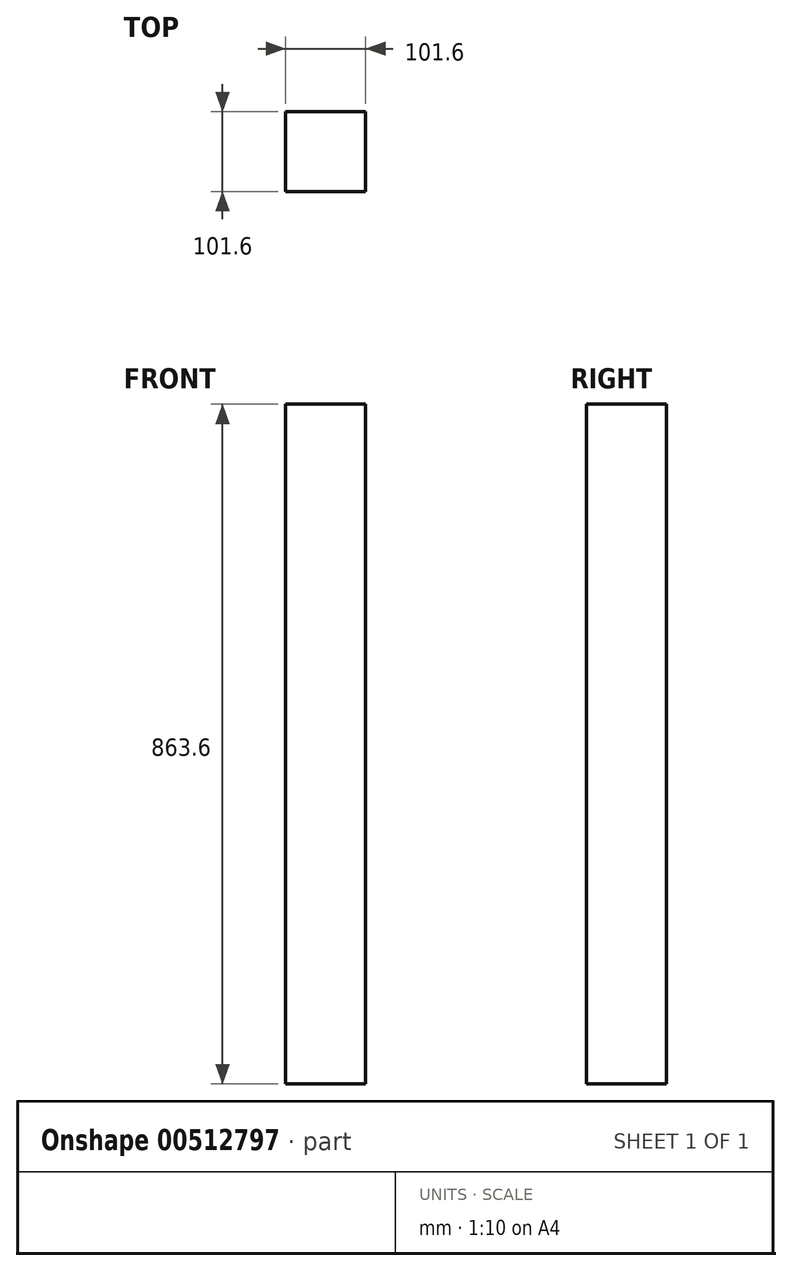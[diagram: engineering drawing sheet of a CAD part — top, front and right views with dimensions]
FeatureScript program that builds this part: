
annotation { "Feature Type Name" : "Feature", "Feature Type Description" : "" }
export const myFeature = defineFeature(function(context is Context, id is Id, definition is map)
    precondition{}
    {
        {
            var Q0;
            Q0=qCreatedBy(makeId("Top.planeOp"),FACE);
            var sketch = newSketch(context, id + "F0", { "sketchPlane" : qUnion([Q0])});
            skLineSegment(sketch, "E0.bottom", {"start": v(-50.8, 50.8) * mm, "end": v(50.8, 50.8) * mm});
            skLineSegment(sketch, "E0.top", {"start": v(-50.8, -50.8) * mm, "end": v(50.8, -50.8) * mm});
            skLineSegment(sketch, "E0.left", {"start": v(-50.8, 50.8) * mm, "end": v(-50.8, -50.8) * mm});
            skLineSegment(sketch, "E0.right", {"start": v(50.8, 50.8) * mm, "end": v(50.8, -50.8) * mm});
            skPoint(sketch, "E0.middle", {"position": v(0, 0) * mm});
            skSolve(sketch);
        }
        {
            var Q0;
            Q0 = qSketchRegion(id + "F0", true);
            extrude(context, id + "F1", {"entities" : qUnion([Q0]), "depth" : 863.6 * mm});
        }
    });
